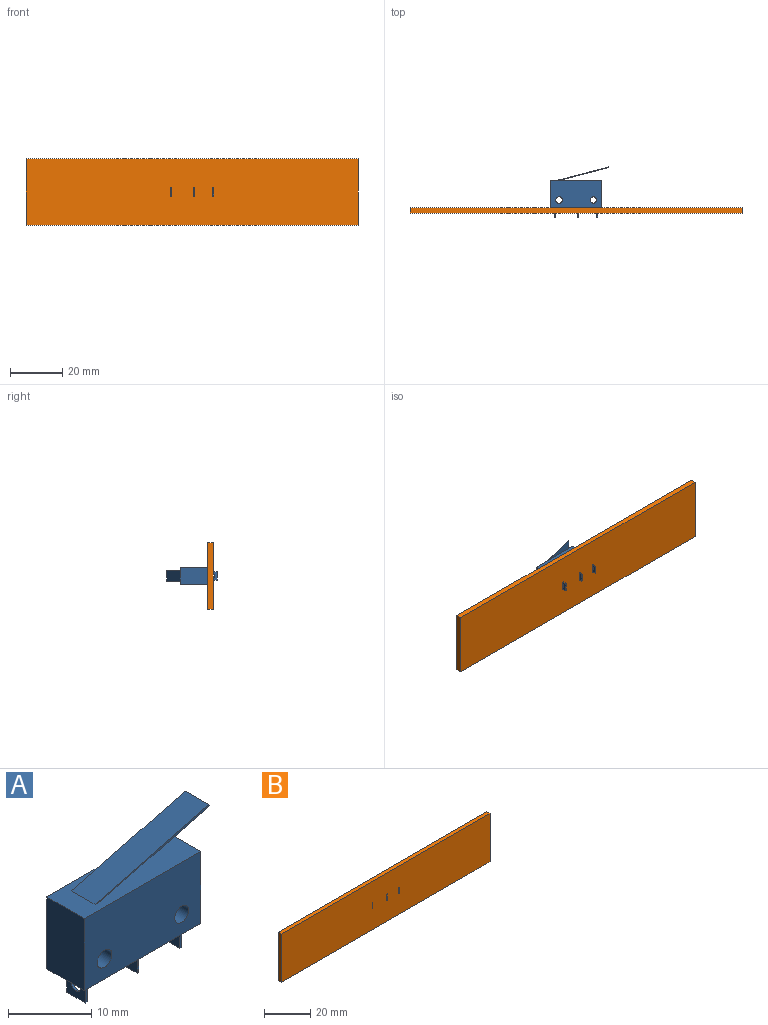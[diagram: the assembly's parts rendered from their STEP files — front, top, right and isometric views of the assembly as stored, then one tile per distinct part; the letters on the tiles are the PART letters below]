
ASSEMBLY  parts=2 mates=1
PART A: 31 faces, bbox 22.4x6.4x19.1 mm
  f0: plane 19.8x6.4mm, normal (0,0,-1), area 123.8mm2, adj f2,f5,f6,f7,f13,f15,f16,f17
  f1: plane 19.8x6.4mm, normal (0,0,1), area 122.8mm2, adj f2,f5,f6,f7,f8,f10,f11,f12
  f2: plane 10.6x6.4mm, normal (1,0,0), area 67.8mm2, adj f0,f1,f6,f7
  f3: cylinder r=1.25mm len=6.4mm, axis (0,1,0), area 50.3mm2, adj f6,f7
  f4: cylinder r=1.2mm len=6.4mm, axis (0,1,0), area 48.3mm2, adj f6,f7
  f5: plane 10.6x6.4mm, normal (-1,0,0), area 67.8mm2, adj f0,f1,f6,f7
  f6: plane 19.8x10.6mm, normal (0,-1,0), area 200.4mm2, adj f0,f1,f2,f3,f4,f5
  f7: plane 19.8x10.6mm, normal (0,1,0), area 200.4mm2, adj f0,f1,f2,f3,f4,f5
  f8: plane 18.43x4.8mm, normal (0.25,0,-0.97), area 76.2mm2, adj f1,f9,f11,f12
  f9: plane 4x0.24mm, normal (0.97,0,0.25), area 1mm2, adj f8,f10,f11,f12
  f10: plane 19.35x5.04mm, normal (-0.25,0,0.97), area 80mm2, adj f1,f9,f11,f12
  f11: plane 19.42x5.04mm, normal (0,-1,0), area 4.9mm2, adj f1,f8,f9,f10
  f12: plane 19.42x5.04mm, normal (0,1,0), area 4.9mm2, adj f1,f8,f9,f10
  f13: plane 3.5x3.2mm, normal (-1,0,0), area 9.4mm2, adj f0,f14,f16,f17,f30
  f14: plane 3.2x0.3mm, normal (0,0,-1), area 1mm2, adj f13,f15,f16,f17
  f15: plane 3.5x3.2mm, normal (1,0,0), area 9.4mm2, adj f0,f14,f16,f17,f30
  f16: plane 3.5x0.3mm, normal (0,-1,0), area 1mm2, adj f0,f13,f14,f15
  f17: plane 3.5x0.3mm, normal (0,1,0), area 1mm2, adj f0,f13,f14,f15
  f18: plane 3.5x3.2mm, normal (1,0,0), area 9.4mm2, adj f0,f20,f21,f22,f29
  f19: plane 3.5x3.2mm, normal (-1,0,0), area 9.4mm2, adj f0,f20,f21,f22,f29
  f20: plane 3.2x0.3mm, normal (0,0,-1), area 1mm2, adj f18,f19,f21,f22
  f21: plane 3.5x0.3mm, normal (0,-1,0), area 1.1mm2, adj f0,f18,f19,f20
  f22: plane 3.5x0.3mm, normal (0,1,0), area 1.1mm2, adj f0,f18,f19,f20
  f23: plane 3.5x3.2mm, normal (1,0,0), area 9.4mm2, adj f0,f25,f26,f27,f28
  f24: plane 3.5x3.2mm, normal (-1,0,0), area 9.4mm2, adj f0,f25,f26,f27,f28
  f25: plane 3.2x0.3mm, normal (0,0,-1), area 1mm2, adj f23,f24,f26,f27
  f26: plane 3.5x0.3mm, normal (0,-1,0), area 1mm2, adj f0,f23,f24,f25
  f27: plane 3.5x0.3mm, normal (0,1,0), area 1mm2, adj f0,f23,f24,f25
  f28: cylinder r=0.75mm len=1.5mm, axis (-1,0,0), area 1.4mm2, adj f23,f24
  f29: cylinder r=0.75mm len=1.5mm, axis (-1,0,0), area 1.4mm2, adj f18,f19
  f30: cylinder r=0.75mm len=1.5mm, axis (-1,0,0), area 1.4mm2, adj f13,f15
PART B: 18 faces, bbox 127x2x25.4 mm
  f0: plane 25.4x2mm, normal (-1,0,0), area 50.8mm2, adj f1,f15,f16,f17
  f1: plane 127x2mm, normal (0,0,-1), area 254mm2, adj f0,f2,f16,f17
  f2: plane 25.4x2mm, normal (1,0,0), area 50.8mm2, adj f1,f15,f16,f17
  f3: plane 3.3x2mm, normal (1,0,0), area 6.6mm2, adj f4,f12,f16,f17
  f4: plane 2x0.25mm, normal (0,0,-1), area 0.5mm2, adj f3,f5,f16,f17
  f5: plane 3.3x2mm, normal (-1,0,0), area 6.6mm2, adj f4,f12,f16,f17
  f6: plane 3.3x2mm, normal (1,0,0), area 6.6mm2, adj f7,f13,f16,f17
  f7: plane 2x0.25mm, normal (0,0,-1), area 0.5mm2, adj f6,f8,f16,f17
  f8: plane 3.3x2mm, normal (-1,0,0), area 6.6mm2, adj f7,f13,f16,f17
  f9: plane 3.3x2mm, normal (1,0,0), area 6.6mm2, adj f10,f14,f16,f17
  f10: plane 2x0.25mm, normal (0,0,-1), area 0.5mm2, adj f9,f11,f16,f17
  f11: plane 3.3x2mm, normal (-1,0,0), area 6.6mm2, adj f10,f14,f16,f17
  f12: plane 2x0.25mm, normal (0,0,1), area 0.5mm2, adj f3,f5,f16,f17
  f13: plane 2x0.25mm, normal (0,0,1), area 0.5mm2, adj f6,f8,f16,f17
  f14: plane 2x0.25mm, normal (0,0,1), area 0.5mm2, adj f9,f11,f16,f17
  f15: plane 127x2mm, normal (0,0,1), area 254mm2, adj f0,f2,f16,f17
  f16: plane 127x25.4mm, normal (0,-1,0), area 3223.3mm2, adj f0,f1,f2,f3,f4,f5,f6,f7
  f17: plane 127x25.4mm, normal (0,1,0), area 3223.3mm2, adj f0,f1,f2,f3,f4,f5,f6,f7
PLACE A rot(axis=(-1,0,0),90deg) t=(0,12.06,3.82)mm
PLACE B rot(axis=(1,0,0),180deg) t=(0,4.76,6.97)mm
MATE fastened B.f16 <-> A.f0  axis (0,1,0) through (0.8,6.76,8.62)mm
